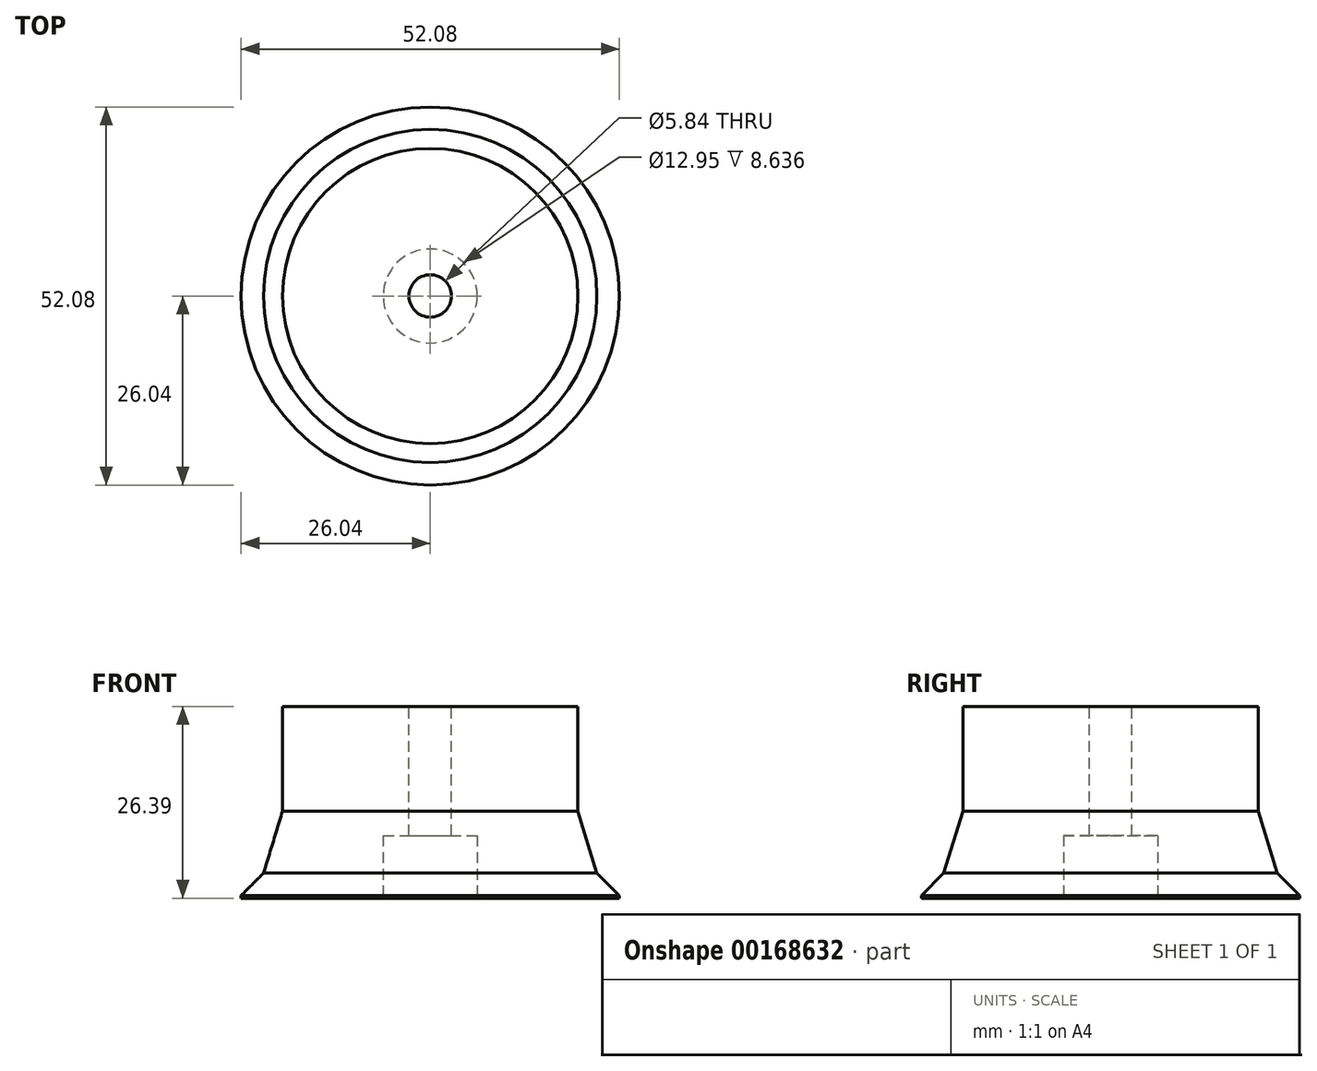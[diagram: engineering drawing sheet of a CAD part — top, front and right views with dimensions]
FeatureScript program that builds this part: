
annotation { "Feature Type Name" : "Feature", "Feature Type Description" : "" }
export const myFeature = defineFeature(function(context is Context, id is Id, definition is map)
    precondition{}
    {
        {
            var Q0;
            Q0=qCreatedBy(makeId("Top.planeOp"),FACE);
            var sketch = newSketch(context, id + "F0", { "sketchPlane" : qUnion([Q0])});
            skCircle(sketch, "E0", {"center": v(0, 0) * mm, "radius": 26.04 * mm});
            skSolve(sketch);
        }
        {
            var Q0;
            Q0 = qSketchRegion(id + "F0", true);
            extrude(context, id + "F1", {"entities" : qUnion([Q0]), "depth" : 4.17 * mm});
        }
        {
            var Q0;
            Q0=makeQuery(id+"F1.opExtrude","CAP_FACE",FACE,{"disambiguationData":[OSD([sQuery(id+"F0.wireOp",EDGE,"E0")])],"isStart":false});
            var sketch = newSketch(context, id + "F2", { "sketchPlane" : qUnion([Q0])});
            skCircle(sketch, "E1", {"center": v(0, 0) * mm, "radius": 22.99 * mm});
            skSolve(sketch);
        }
        {
            var Q0;
            Q0 = qSketchRegion(id + "F2", true);
            extrude(context, id + "F3", {"entities" : qUnion([Q0]), "operationType" : NewBodyOperationType.ADD, "depth" : 8.25 * mm});
        }
        {
            var Q0;
            Q0=makeQuery(id+"F3.opExtrude","CAP_FACE",FACE,{"disambiguationData":[OSD([sQuery(id+"F2.wireOp",EDGE,"E1")])],"isStart":false});
            var sketch = newSketch(context, id + "F4", { "sketchPlane" : qUnion([Q0])});
            skCircle(sketch, "E2", {"center": v(0, 0) * mm, "radius": 20.32 * mm});
            skSolve(sketch);
        }
        {
            var Q0;
            Q0=makeQuery(id+"F4.imprint","IMPRINT",FACE,{"disambiguationData":[TD([[makeQuery(id+"F4.imprint","IMPRINT",EDGE,{"derivedFrom":sQuery(id+"F4.wireOp",EDGE,"E2")}),1.0]])]});
            extrude(context, id + "F5", {"entities" : qUnion([Q0]), "operationType" : NewBodyOperationType.ADD, "depth" : 13.97 * mm});
        }
        {
            var Q0;
            Q0=makeQuery(id+"F1.opExtrude","CAP_EDGE",EDGE,{"disambiguationData":[OSD([sQuery(id+"F0.wireOp",EDGE,"E0")])],"isStart":false});
            chamfer(context, id + "F6", {"entities" : qUnion([Q0]), "width" : 3.8 * mm, "tangentPropagation" : true});
        }
        {
            var Q0;
            Q0=makeQuery(id+"F3.opExtrude","CAP_EDGE",EDGE,{"disambiguationData":[OSD([sQuery(id+"F2.wireOp",EDGE,"E1")])],"isStart":false});
            chamfer(context, id + "F7", {"entities" : qUnion([Q0]), "chamferType" : ChamferType.OFFSET_ANGLE, "width" : 2.8 * mm, "oppositeDirection" : false, "angle" : 73 * degree, "tangentPropagation" : true});
        }
        {
            var Q0;
            Q0=makeQuery(id+"F5.opExtrude","CAP_FACE",FACE,{"disambiguationData":[OSD([sQuery(id+"F4.wireOp",EDGE,"E2")])],"isStart":false});
            var sketch = newSketch(context, id + "F8", { "sketchPlane" : qUnion([Q0])});
            skCircle(sketch, "E3", {"center": v(0, 0) * mm, "radius": 2.92 * mm});
            skSolve(sketch);
        }
        {
            var Q0;
            Q0=makeQuery(id+"F8.imprint","IMPRINT",FACE,{"disambiguationData":[TD([[makeQuery(id+"F8.imprint","IMPRINT",EDGE,{"derivedFrom":sQuery(id+"F8.wireOp",EDGE,"E3")}),1.0]])]});
            extrude(context, id + "F9", {"entities" : qUnion([Q0]), "operationType" : NewBodyOperationType.REMOVE, "endBound" : BoundingType.THROUGH_ALL, "oppositeDirection" : true, "depth" : 25.4 * mm});
        }
        {
            var Q0;
            Q0=makeQuery(id+"F1.opExtrude","CAP_FACE",FACE,{"disambiguationData":[OSD([sQuery(id+"F0.wireOp",EDGE,"E0")])],"isStart":true});
            var sketch = newSketch(context, id + "F10", { "sketchPlane" : qUnion([Q0])});
            skCircle(sketch, "E4", {"center": v(0, 0) * mm, "radius": 6.48 * mm});
            skSolve(sketch);
        }
        {
            var Q0;
            Q0 = qSketchRegion(id + "F10", true);
            extrude(context, id + "F11", {"entities" : qUnion([Q0]), "operationType" : NewBodyOperationType.REMOVE, "oppositeDirection" : true, "depth" : 8.64 * mm});
        }
    });
